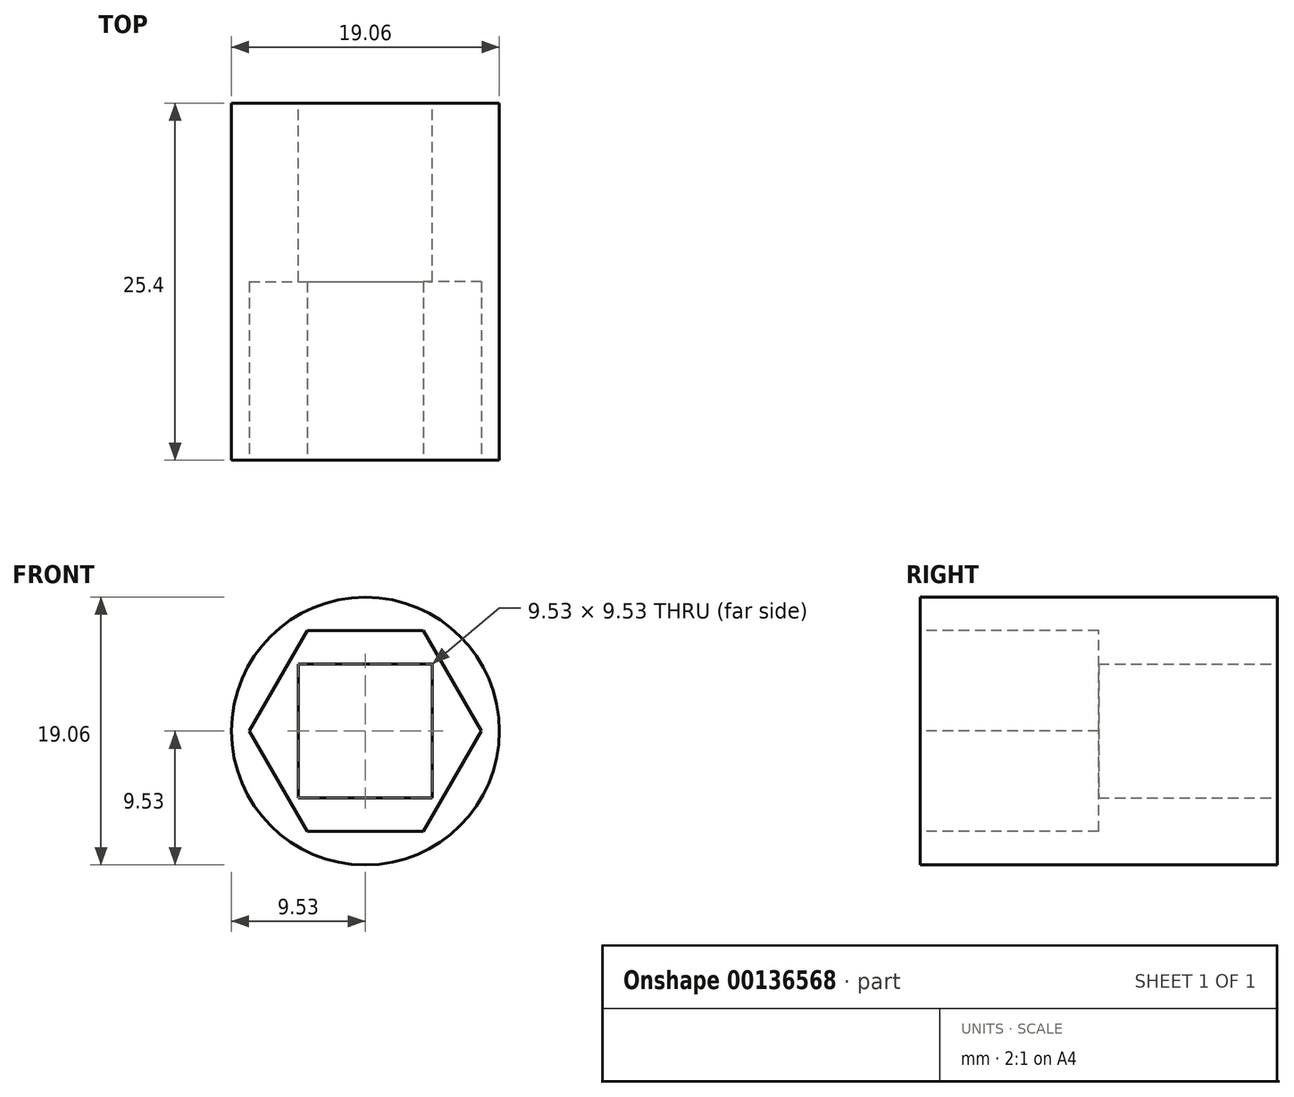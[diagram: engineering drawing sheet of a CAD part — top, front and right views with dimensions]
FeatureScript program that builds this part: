
annotation { "Feature Type Name" : "Feature", "Feature Type Description" : "" }
export const myFeature = defineFeature(function(context is Context, id is Id, definition is map)
    precondition{}
    {
        {
            var Q0;
            Q0=qCreatedBy(makeId("Front.planeOp"),FACE);
            var sketch = newSketch(context, id + "F0", { "sketchPlane" : qUnion([Q0])});
            skCircle(sketch, "E0", {"center": v(0, 0) * mm, "radius": 9.53 * mm});
            skSolve(sketch);
        }
        {
            var Q0;
            Q0 = qSketchRegion(id + "F0", true);
            extrude(context, id + "F1", {"entities" : qUnion([Q0]), "depth" : 25.4 * mm});
        }
        {
            var Q0;
            Q0=qCreatedBy(makeId("Front.planeOp"),FACE);
            var sketch = newSketch(context, id + "F2", { "sketchPlane" : qUnion([Q0])});
            skLineSegment(sketch, "E1.bottom", {"start": v(-4.76, 4.76) * mm, "end": v(4.76, 4.76) * mm});
            skLineSegment(sketch, "E1.top", {"start": v(-4.76, -4.76) * mm, "end": v(4.76, -4.76) * mm});
            skLineSegment(sketch, "E1.left", {"start": v(-4.76, 4.76) * mm, "end": v(-4.76, -4.76) * mm});
            skLineSegment(sketch, "E1.right", {"start": v(4.76, 4.76) * mm, "end": v(4.76, -4.76) * mm});
            skPoint(sketch, "E1.middle", {"position": v(0, 0) * mm});
            skCircle(sketch, "E2", {"center": v(0, 0) * mm, "radius": 4.76 * mm});
            skSolve(sketch);
        }
        {
            var Q0;
            {var subQ0=sQuery(id+"F2.wireOp",EDGE,"E2");var subQ1=makeQuery(id+"F2.imprint","INTERSECT",VERTEX,{"derivedFrom":[sQuery(id+"F2.wireOp",EDGE,"E1.bottom"),subQ0]});Q0=makeQuery(id+"F2.imprint","IMPRINT",FACE,{"disambiguationData":[TD([[makeQuery(id+"F2.imprint","IMPRINT",EDGE,{"disambiguationData":[TD([[subQ1,1.0]])],"derivedFrom":subQ0}),1.0]])]});}
            extrude(context, id + "F3", {"entities" : qUnion([Q0]), "operationType" : NewBodyOperationType.REMOVE, "endBound" : BoundingType.THROUGH_ALL, "depth" : 25.4 * mm});
        }
        {
            var Q0;
            {var subQ0=sQuery(id+"F2.wireOp",EDGE,"E1.right");var subQ1=sQuery(id+"F2.wireOp",EDGE,"E1.top");var subQ2=makeQuery(id+"F2.imprint","INTERSECT",VERTEX,{"derivedFrom":[subQ1,subQ0]});Q0=makeQuery(id+"F2.imprint","IMPRINT",FACE,{"disambiguationData":[TD([[makeQuery(id+"F2.imprint","IMPRINT",EDGE,{"disambiguationData":[TD([[subQ2,1.0]])],"derivedFrom":subQ1}),1.0]])]});}
            var Q1;
            {var subQ0=sQuery(id+"F2.wireOp",EDGE,"E1.right");var subQ1=sQuery(id+"F2.wireOp",EDGE,"E1.bottom");var subQ2=makeQuery(id+"F2.imprint","INTERSECT",VERTEX,{"derivedFrom":[subQ1,subQ0]});Q1=makeQuery(id+"F2.imprint","IMPRINT",FACE,{"disambiguationData":[TD([[makeQuery(id+"F2.imprint","IMPRINT",EDGE,{"disambiguationData":[TD([[subQ2,1.0]])],"derivedFrom":subQ1}),-1.0]])]});}
            var Q2;
            {var subQ0=sQuery(id+"F2.wireOp",EDGE,"E1.left");var subQ1=sQuery(id+"F2.wireOp",EDGE,"E1.bottom");var subQ2=makeQuery(id+"F2.imprint","INTERSECT",VERTEX,{"derivedFrom":[subQ1,subQ0]});Q2=makeQuery(id+"F2.imprint","IMPRINT",FACE,{"disambiguationData":[TD([[makeQuery(id+"F2.imprint","IMPRINT",EDGE,{"disambiguationData":[TD([[subQ2,-1.0]])],"derivedFrom":subQ1}),-1.0]])]});}
            var Q3;
            {var subQ0=sQuery(id+"F2.wireOp",EDGE,"E1.left");var subQ1=sQuery(id+"F2.wireOp",EDGE,"E1.top");var subQ2=makeQuery(id+"F2.imprint","INTERSECT",VERTEX,{"derivedFrom":[subQ1,subQ0]});Q3=makeQuery(id+"F2.imprint","IMPRINT",FACE,{"disambiguationData":[TD([[makeQuery(id+"F2.imprint","IMPRINT",EDGE,{"disambiguationData":[TD([[subQ2,-1.0]])],"derivedFrom":subQ1}),1.0]])]});}
            extrude(context, id + "F4", {"entities" : qUnion([Q0, Q1, Q2, Q3]), "operationType" : NewBodyOperationType.REMOVE, "depth" : 12.7 * mm});
        }
        {
            var Q0;
            Q0=makeQuery(id+"F1.opExtrude","CAP_FACE",FACE,{"disambiguationData":[OSD([sQuery(id+"F0.wireOp",EDGE,"E0")])],"isStart":false});
            var sketch = newSketch(context, id + "F5", { "sketchPlane" : qUnion([Q0])});
            skCircle(sketch, "E3.cCircle", {"center": v(0, 0) * mm, "radius": 7.15 * mm, "construction": true});
            skLineSegment(sketch, "E3.0", {"start": v(-4.13, 7.15) * mm, "end": v(4.13, 7.15) * mm});
            skLineSegment(sketch, "E3.1", {"start": v(4.13, 7.15) * mm, "end": v(8.26, 0) * mm});
            skLineSegment(sketch, "E3.2", {"start": v(8.25, 0) * mm, "end": v(4.13, -7.15) * mm});
            skLineSegment(sketch, "E3.3", {"start": v(4.13, -7.15) * mm, "end": v(-4.13, -7.15) * mm});
            skLineSegment(sketch, "E3.4", {"start": v(-4.13, -7.15) * mm, "end": v(-8.26, 0) * mm});
            skLineSegment(sketch, "E3.5", {"start": v(-8.25, 0) * mm, "end": v(-4.13, 7.15) * mm});
            skPoint(sketch, "E3.0.midPoint", {"position": v(0, 7.15) * mm});
            skSolve(sketch);
        }
        {
            var Q0;
            Q0=makeQuery(id+"F5.imprint","IMPRINT",FACE,{"disambiguationData":[TD([[makeQuery(id+"F5.imprint","IMPRINT",EDGE,{"derivedFrom":sQuery(id+"F5.wireOp",EDGE,"E3.0")}),-1.0]])]});
            extrude(context, id + "F6", {"entities" : qUnion([Q0]), "operationType" : NewBodyOperationType.REMOVE, "oppositeDirection" : true, "depth" : 12.7 * mm});
        }
    });
